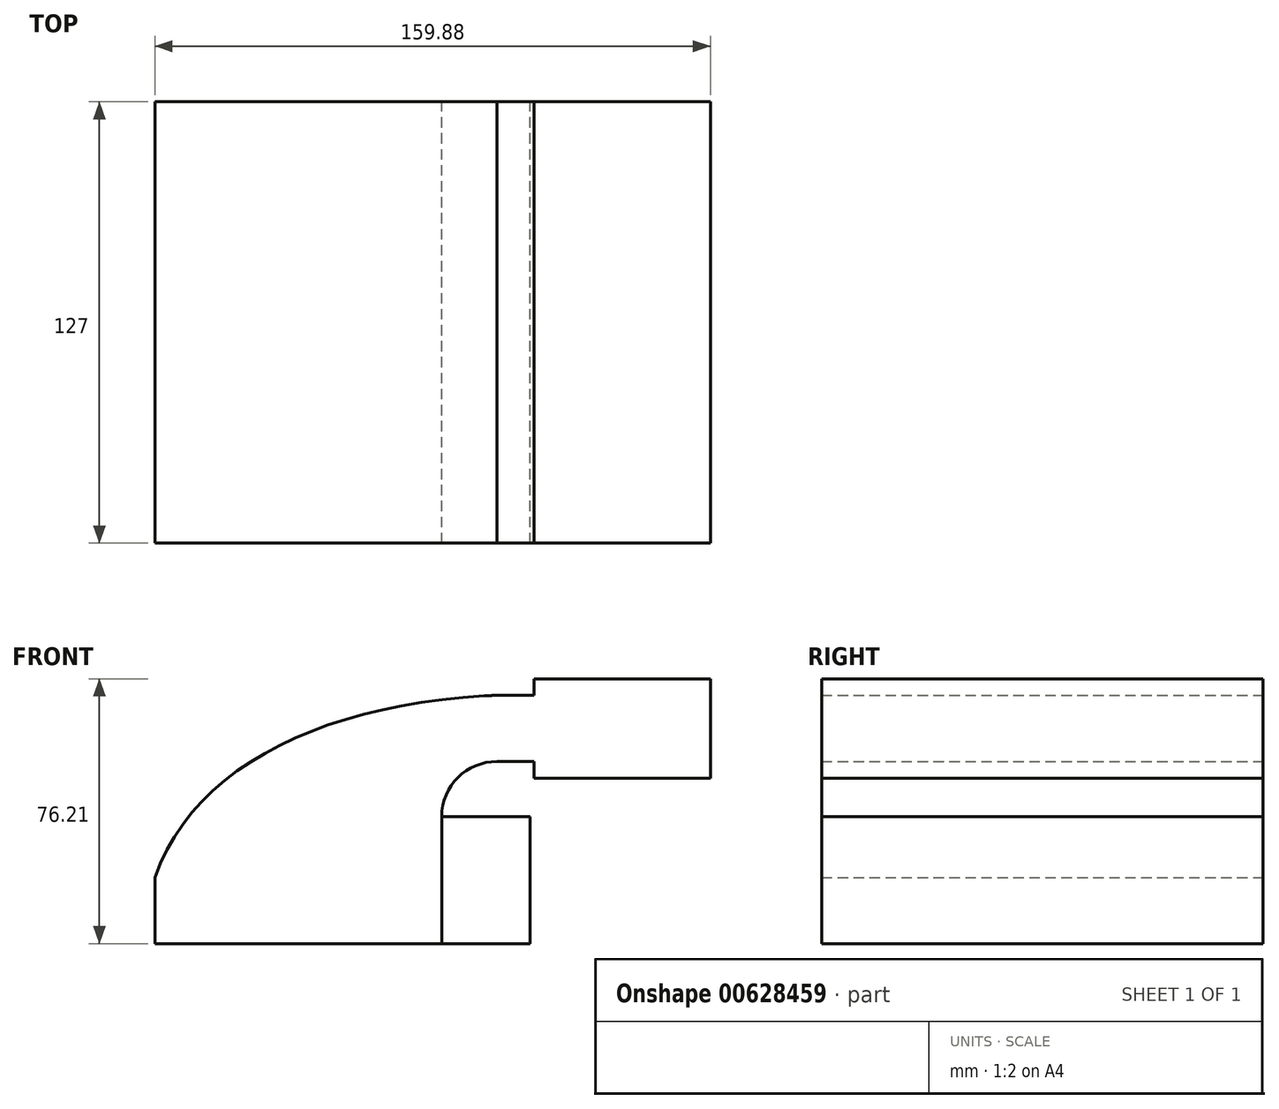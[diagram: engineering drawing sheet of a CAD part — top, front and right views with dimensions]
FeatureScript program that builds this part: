
annotation { "Feature Type Name" : "Feature", "Feature Type Description" : "" }
export const myFeature = defineFeature(function(context is Context, id is Id, definition is map)
    precondition{}
    {
        {
            var Q0;
            Q0=qCreatedBy(makeId("Front.planeOp"),FACE);
            var sketch = newSketch(context, id + "F0", { "sketchPlane" : qUnion([Q0])});
            skLineSegment(sketch, "E0.bottom", {"start": v(-41.28, -9.53) * mm, "end": v(41.28, -9.53) * mm});
            skLineSegment(sketch, "E0.top", {"start": v(-41.28, 9.53) * mm, "end": v(41.28, 9.53) * mm});
            skLineSegment(sketch, "E0.left", {"start": v(-41.28, -9.53) * mm, "end": v(-41.28, 9.53) * mm});
            skLineSegment(sketch, "E0.right", {"start": v(41.28, -9.53) * mm, "end": v(41.28, 9.53) * mm});
            skPoint(sketch, "E0.middle", {"position": v(0, 0) * mm});
            skLineSegment(sketch, "E1.bottom", {"start": v(118.6, 38.1) * mm, "end": v(67.8, 38.1) * mm});
            skLineSegment(sketch, "E1.top", {"start": v(118.6, 66.68) * mm, "end": v(67.8, 66.68) * mm});
            skLineSegment(sketch, "E1.left", {"start": v(118.6, 38.1) * mm, "end": v(118.6, 66.68) * mm});
            skLineSegment(sketch, "E1.right", {"start": v(67.8, 38.1) * mm, "end": v(67.8, 66.68) * mm});
            skPoint(sketch, "E1.middle", {"position": v(93.2, 52.39) * mm});
            skLineSegment(sketch, "E2", {"start": v(41.28, 9.53) * mm, "end": v(41.28, 27) * mm});
            skArc(sketch, "E3", {"start": v(41.27, 27) * mm, "mid": v(45.92, 38.23) * mm, "end": v(57.15, 42.88) * mm});
            skLineSegment(sketch, "E4", {"start": v(57.15, 42.88) * mm, "end": v(79.08, 42.88) * mm});
            skLineSegment(sketch, "E5.0", {"start": v(57.15, 61.93) * mm, "end": v(79.08, 61.93) * mm});
            skArc(sketch, "E5.1", {"start": v(22.23, 27) * mm, "mid": v(32.45, 51.7) * mm, "end": v(57.15, 61.93) * mm});
            skLineSegment(sketch, "E5.2", {"start": v(22.22, 9.53) * mm, "end": v(22.22, 27) * mm});
            skFitSpline(sketch, "E6", {"points": [v(-41.28, 9.53) * mm, v(57.15, 61.93) * mm], "startDerivative": vector(33.93, 96.94) * mm, "endDerivative": vector(147.97, 6.54) * mm});
            skFitSpline(sketch, "E7", {"points": [v(58.43, 60.72) * mm, v(57.15, 61.93) * mm], "startDerivative": vector(-1.28, 1.2) * mm, "endDerivative": vector(-1.28, 1.2) * mm});
            skSolve(sketch);
        }
        {
            var Q0;
            {var subQ3=sQuery(id+"F0.wireOp",EDGE,"E5.2");Q0=makeQuery(id+"F0.imprint","IMPRINT",FACE,{"disambiguationData":[TD([[makeQuery(id+"F0.imprint","IMPRINT",EDGE,{"derivedFrom":subQ3}),1.0]])]});}
            var Q1;
            {var subQ0=sQuery(id+"F0.wireOp",EDGE,"E2");Q1=makeQuery(id+"F0.imprint","IMPRINT",FACE,{"disambiguationData":[TD([[makeQuery(id+"F0.imprint","IMPRINT",EDGE,{"derivedFrom":subQ0}),1.0]])]});}
            var Q2;
            {var subQ1=sQuery(id+"F0.wireOp",EDGE,"E1.bottom");Q2=makeQuery(id+"F0.imprint","IMPRINT",FACE,{"disambiguationData":[TD([[makeQuery(id+"F0.imprint","IMPRINT",EDGE,{"derivedFrom":subQ1}),-1.0]])]});}
            var Q3;
            Q3=makeQuery(id+"F0.imprint","IMPRINT",FACE,{"disambiguationData":[TD([[makeQuery(id+"F0.imprint","IMPRINT",EDGE,{"derivedFrom":sQuery(id+"F0.wireOp",EDGE,"E0.bottom")}),1.0]])]});
            extrude(context, id + "F1", {"entities" : qUnion([Q0, Q1, Q2, Q3]), "endBound" : BoundingType.SYMMETRIC, "depth" : 127 * mm, "offsetDistance" : 25.4 * mm});
        }
        {
            var Q0;
            Q0=makeQuery(id+"F1.opExtrude","SWEPT_FACE",FACE,{"disambiguationData":[OSD([sQuery(id+"F0.wireOp",EDGE,"E0.right"),sQuery(id+"F0.wireOp",EDGE,"E2")])]});
            extrude(context, id + "F2", {"entities" : qUnion([Q0]), "depth" : 25.4 * mm, "offsetDistance" : 25.4 * mm});
        }
    });
